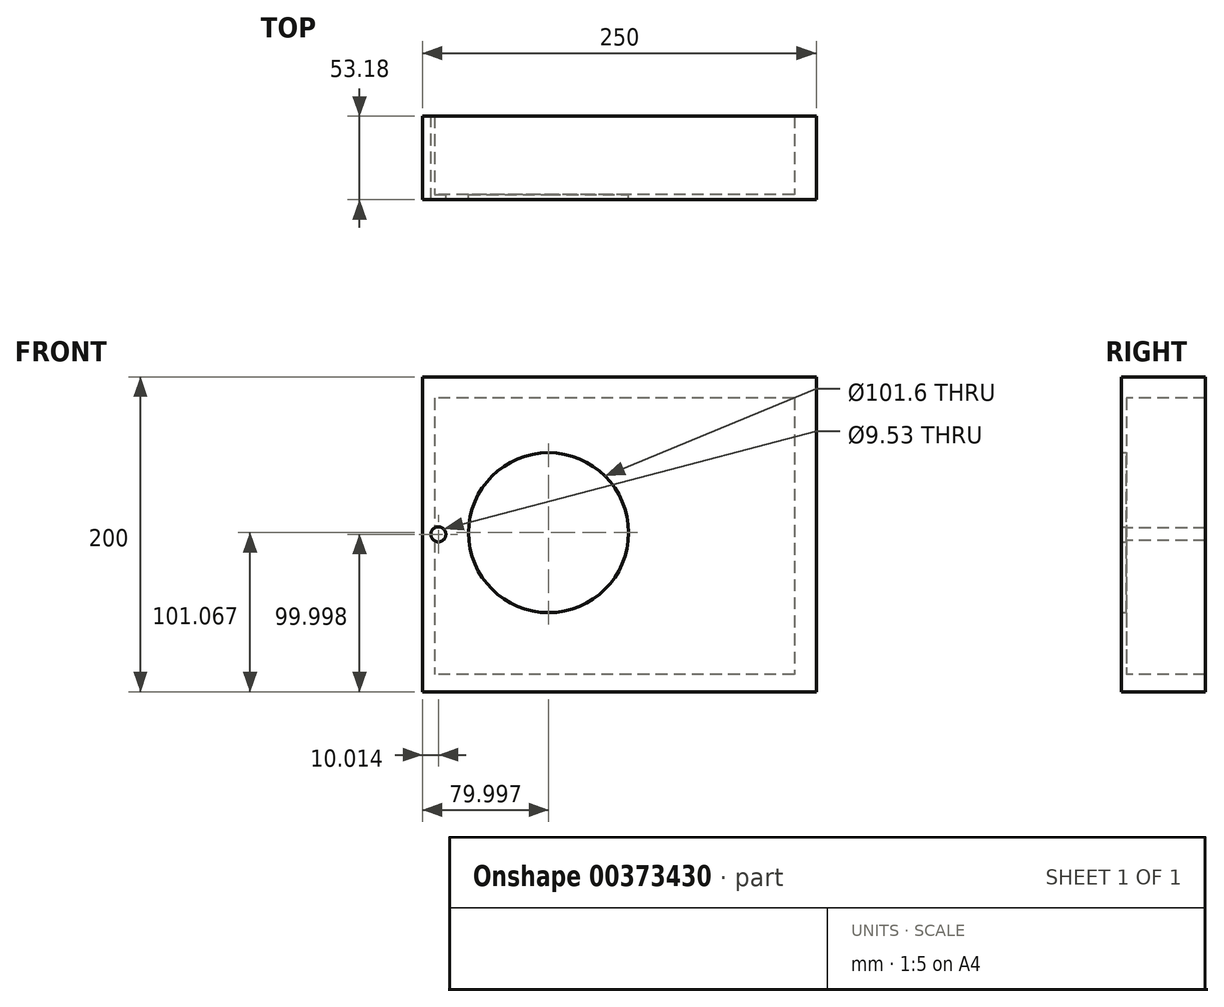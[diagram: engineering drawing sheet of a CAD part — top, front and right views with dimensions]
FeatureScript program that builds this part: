
annotation { "Feature Type Name" : "Feature", "Feature Type Description" : "" }
export const myFeature = defineFeature(function(context is Context, id is Id, definition is map)
    precondition{}
    {
        {
            var Q0;
            Q0=qCreatedBy(makeId("Front.planeOp"),FACE);
            var sketch = newSketch(context, id + "F0", { "sketchPlane" : qUnion([Q0])});
            skLineSegment(sketch, "E0.bottom", {"start": v(-154.06, 7.63) * mm, "end": v(95.94, 7.63) * mm});
            skLineSegment(sketch, "E0.top", {"start": v(-154.06, -192.37) * mm, "end": v(95.94, -192.37) * mm});
            skLineSegment(sketch, "E0.left", {"start": v(-154.06, 7.63) * mm, "end": v(-154.06, -192.37) * mm});
            skLineSegment(sketch, "E0.right", {"start": v(95.94, 7.63) * mm, "end": v(95.94, -192.37) * mm});
            skCircle(sketch, "E1", {"center": v(-74.06, -91.3) * mm, "radius": 50.8 * mm});
            skLineSegment(sketch, "E2.bottom", {"start": v(28.34, -18.93) * mm, "end": v(78.34, -18.93) * mm, "construction": true});
            skLineSegment(sketch, "E2.top", {"start": v(28.34, -157.98) * mm, "end": v(78.34, -157.98) * mm, "construction": true});
            skLineSegment(sketch, "E2.left", {"start": v(28.34, -18.93) * mm, "end": v(28.34, -157.98) * mm, "construction": true});
            skLineSegment(sketch, "E2.right", {"start": v(78.34, -18.93) * mm, "end": v(78.34, -157.98) * mm, "construction": true});
            skCircle(sketch, "E3", {"center": v(-144.05, -92.37) * mm, "radius": 4.76 * mm});
            skPoint(sketch, "E3.centerSnap0", {"position": v(-154.06, -92.37) * mm});
            skSolve(sketch);
        }
        {
            var Q0;
            Q0=makeQuery(id+"F0.imprint","IMPRINT",FACE,{"disambiguationData":[TD([[makeQuery(id+"F0.imprint","IMPRINT",EDGE,{"derivedFrom":sQuery(id+"F0.wireOp",EDGE,"E0.bottom")}),-1.0]])]});
            extrude(context, id + "F1", {"entities" : qUnion([Q0]), "depth" : 3.17 * mm});
        }
        {
            var Q0;
            Q0=makeQuery(id+"F1.opExtrude","CAP_FACE",FACE,{"disambiguationData":[OSD([sQuery(id+"F0.wireOp",EDGE,"E0.bottom"),sQuery(id+"F0.wireOp",EDGE,"E0.top"),sQuery(id+"F0.wireOp",EDGE,"E0.left"),sQuery(id+"F0.wireOp",EDGE,"E0.right"),sQuery(id+"F0.wireOp",EDGE,"E1"),sQuery(id+"F0.wireOp",EDGE,"E2.bottom"),sQuery(id+"F0.wireOp",EDGE,"E2.top"),sQuery(id+"F0.wireOp",EDGE,"E2.left"),sQuery(id+"F0.wireOp",EDGE,"E2.right")])],"isStart":true});
            var sketch = newSketch(context, id + "F2", { "sketchPlane" : qUnion([Q0])});
            skLineSegment(sketch, "E4.bottom", {"start": v(-95.94, 7.63) * mm, "end": v(154.06, 7.63) * mm});
            skLineSegment(sketch, "E4.top", {"start": v(-95.94, -192.37) * mm, "end": v(154.06, -192.37) * mm});
            skLineSegment(sketch, "E4.left", {"start": v(-95.94, 7.63) * mm, "end": v(-95.94, -192.37) * mm});
            skLineSegment(sketch, "E4.right", {"start": v(154.06, 7.63) * mm, "end": v(154.06, -192.37) * mm});
            skLineSegment(sketch, "E5.bottom", {"start": v(-82, -5.91) * mm, "end": v(146.54, -5.91) * mm});
            skLineSegment(sketch, "E5.top", {"start": v(-82, -181.33) * mm, "end": v(146.54, -181.33) * mm});
            skLineSegment(sketch, "E5.left", {"start": v(-82, -5.91) * mm, "end": v(-82, -181.33) * mm});
            skLineSegment(sketch, "E5.right", {"start": v(146.54, -5.91) * mm, "end": v(146.54, -181.33) * mm});
            skSolve(sketch);
        }
        {
            var Q0;
            Q0=makeQuery(id+"F2.imprint","IMPRINT",FACE,{"disambiguationData":[TD([[makeQuery(id+"F2.imprint","IMPRINT",EDGE,{"derivedFrom":sQuery(id+"F2.wireOp",EDGE,"E4.bottom")}),1.0]])]});
            extrude(context, id + "F3", {"entities" : qUnion([Q0]), "operationType" : NewBodyOperationType.ADD, "depth" : 50 * mm});
        }
    });
